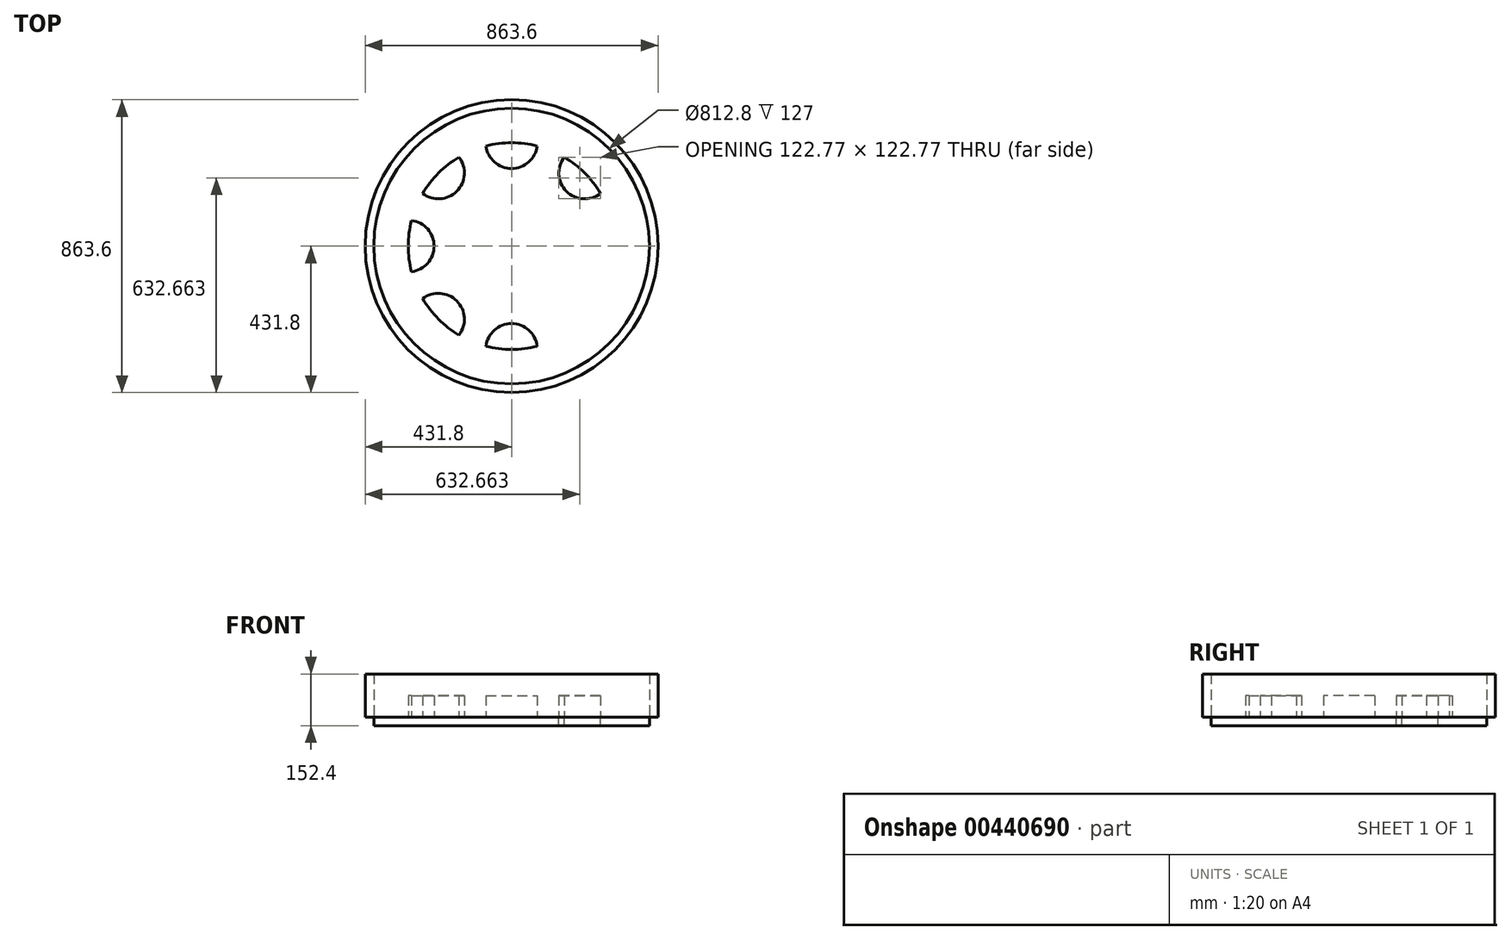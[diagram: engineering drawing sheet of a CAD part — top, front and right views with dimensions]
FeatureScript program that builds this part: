
annotation { "Feature Type Name" : "Feature", "Feature Type Description" : "" }
export const myFeature = defineFeature(function(context is Context, id is Id, definition is map)
    precondition{}
    {
        {
            var Q0;
            Q0=qCreatedBy(makeId("Top.planeOp"),FACE);
            var sketch = newSketch(context, id + "F0", { "sketchPlane" : qUnion([Q0])});
            skCircle(sketch, "E0", {"center": v(0, 0) * mm, "radius": 304.8 * mm});
            skSolve(sketch);
        }
        {
            var Q0;
            Q0=makeQuery(id+"F0.imprint","IMPRINT",FACE,{"disambiguationData":[TD([[makeQuery(id+"F0.imprint","IMPRINT",EDGE,{"derivedFrom":sQuery(id+"F0.wireOp",EDGE,"E0")}),1.0]])]});
            extrude(context, id + "F1", {"entities" : qUnion([Q0]), "depth" : 63.5 * mm});
        }
        {
            var Q0;
            Q0=makeQuery(id+"F1.opExtrude","CAP_FACE",FACE,{"disambiguationData":[OSD([sQuery(id+"F0.wireOp",EDGE,"E0")])],"isStart":true});
            var sketch = newSketch(context, id + "F2", { "sketchPlane" : qUnion([Q0])});
            skCircle(sketch, "E1", {"center": v(0, 304.8) * mm, "radius": 76.2 * mm});
            skCircle(sketch, "E2.1.0", {"center": v(215.53, 215.53) * mm, "radius": 76.2 * mm});
            skCircle(sketch, "E2.2.0", {"center": v(304.8, 0) * mm, "radius": 76.2 * mm});
            skPoint(sketch, "E2.center", {"position": v(0, 0) * mm});
            skLineSegment(sketch, "E2.anchor1", {"start": v(0, 0) * mm, "end": v(0, 304.8) * mm, "construction": true});
            skLineSegment(sketch, "E2.anchor2", {"start": v(0, 0) * mm, "end": v(304.8, 0) * mm, "construction": true});
            skCircle(sketch, "E3.1.0", {"center": v(215.53, -215.53) * mm, "radius": 76.2 * mm});
            skCircle(sketch, "E3.2.0", {"center": v(0, -304.8) * mm, "radius": 76.2 * mm});
            skLineSegment(sketch, "E3.anchor2", {"start": v(0, 0) * mm, "end": v(0, -304.8) * mm, "construction": true});
            skCircle(sketch, "E4.MirrorC", {"center": v(-215.53, 215.53) * mm, "radius": 76.2 * mm});
            skCircle(sketch, "E5.MirrorC", {"center": v(-304.8, 0) * mm, "radius": 76.2 * mm});
            skCircle(sketch, "E6.MirrorC", {"center": v(-215.53, -215.53) * mm, "radius": 76.2 * mm});
            skSolve(sketch);
        }
        {
            var Q0;
            {var subQ0=sQuery(id+"F2.wireOp",EDGE,"E1");var subQ1=makeQuery(id+"F1.opExtrude","CAP_EDGE",EDGE,{"disambiguationData":[OSD([sQuery(id+"F0.wireOp",EDGE,"E0")])],"isStart":true});var subQ2=makeQuery(id+"F2.imprint","INTERSECT",VERTEX,{"disambiguationData":[OD(0.0)],"derivedFrom":[subQ1,subQ0]});Q0=makeQuery(id+"F2.imprint","IMPRINT",FACE,{"disambiguationData":[TD([[makeQuery(id+"F2.imprint","IMPRINT",EDGE,{"disambiguationData":[TD([[subQ2,-1.0]])],"derivedFrom":subQ0}),-1.0]])]});}
            var Q1;
            {var subQ0=sQuery(id+"F2.wireOp",EDGE,"E4.MirrorC");var subQ1=makeQuery(id+"F1.opExtrude","CAP_EDGE",EDGE,{"disambiguationData":[OSD([sQuery(id+"F0.wireOp",EDGE,"E0")])],"isStart":true});var subQ2=makeQuery(id+"F2.imprint","INTERSECT",VERTEX,{"disambiguationData":[OD(0.0)],"derivedFrom":[subQ1,subQ0]});Q1=makeQuery(id+"F2.imprint","IMPRINT",FACE,{"disambiguationData":[TD([[makeQuery(id+"F2.imprint","IMPRINT",EDGE,{"disambiguationData":[TD([[subQ2,-1.0]])],"derivedFrom":subQ0}),-1.0]])]});}
            var Q2;
            {var subQ0=sQuery(id+"F2.wireOp",EDGE,"E5.MirrorC");var subQ1=makeQuery(id+"F1.opExtrude","CAP_EDGE",EDGE,{"disambiguationData":[OSD([sQuery(id+"F0.wireOp",EDGE,"E0")])],"isStart":true});var subQ2=makeQuery(id+"F2.imprint","INTERSECT",VERTEX,{"disambiguationData":[OD(0.0)],"derivedFrom":[subQ1,subQ0]});Q2=makeQuery(id+"F2.imprint","IMPRINT",FACE,{"disambiguationData":[TD([[makeQuery(id+"F2.imprint","IMPRINT",EDGE,{"disambiguationData":[TD([[subQ2,-1.0]])],"derivedFrom":subQ0}),-1.0]])]});}
            var Q3;
            {var subQ0=sQuery(id+"F2.wireOp",EDGE,"E6.MirrorC");var subQ1=makeQuery(id+"F1.opExtrude","CAP_EDGE",EDGE,{"disambiguationData":[OSD([sQuery(id+"F0.wireOp",EDGE,"E0")])],"isStart":true});var subQ2=makeQuery(id+"F2.imprint","INTERSECT",VERTEX,{"disambiguationData":[OD(0.0)],"derivedFrom":[subQ1,subQ0]});Q3=makeQuery(id+"F2.imprint","IMPRINT",FACE,{"disambiguationData":[TD([[makeQuery(id+"F2.imprint","IMPRINT",EDGE,{"disambiguationData":[TD([[subQ2,-1.0]])],"derivedFrom":subQ0}),-1.0]])]});}
            var Q4;
            {var subQ0=sQuery(id+"F2.wireOp",EDGE,"E3.2.0");var subQ1=makeQuery(id+"F1.opExtrude","CAP_EDGE",EDGE,{"disambiguationData":[OSD([sQuery(id+"F0.wireOp",EDGE,"E0")])],"isStart":true});var subQ2=makeQuery(id+"F2.imprint","INTERSECT",VERTEX,{"disambiguationData":[OD(0.0)],"derivedFrom":[subQ1,subQ0]});Q4=makeQuery(id+"F2.imprint","IMPRINT",FACE,{"disambiguationData":[TD([[makeQuery(id+"F2.imprint","IMPRINT",EDGE,{"disambiguationData":[TD([[subQ2,-1.0]])],"derivedFrom":subQ0}),1.0]])]});}
            var Q5;
            {var subQ0=sQuery(id+"F2.wireOp",EDGE,"E3.1.0");var subQ1=makeQuery(id+"F1.opExtrude","CAP_EDGE",EDGE,{"disambiguationData":[OSD([sQuery(id+"F0.wireOp",EDGE,"E0")])],"isStart":true});var subQ2=makeQuery(id+"F2.imprint","INTERSECT",VERTEX,{"disambiguationData":[OD(0.0)],"derivedFrom":[subQ1,subQ0]});Q5=makeQuery(id+"F2.imprint","IMPRINT",FACE,{"disambiguationData":[TD([[makeQuery(id+"F2.imprint","IMPRINT",EDGE,{"disambiguationData":[TD([[subQ2,-1.0]])],"derivedFrom":subQ0}),1.0]])]});}
            var Q6;
            {var subQ0=sQuery(id+"F2.wireOp",EDGE,"E2.2.0");var subQ1=makeQuery(id+"F1.opExtrude","CAP_EDGE",EDGE,{"disambiguationData":[OSD([sQuery(id+"F0.wireOp",EDGE,"E0")])],"isStart":true});var subQ2=makeQuery(id+"F2.imprint","INTERSECT",VERTEX,{"disambiguationData":[OD(0.0)],"derivedFrom":[subQ1,subQ0]});Q6=makeQuery(id+"F2.imprint","IMPRINT",FACE,{"disambiguationData":[TD([[makeQuery(id+"F2.imprint","IMPRINT",EDGE,{"disambiguationData":[TD([[subQ2,-1.0]])],"derivedFrom":subQ0}),1.0]])]});}
            var Q7;
            {var subQ0=sQuery(id+"F2.wireOp",EDGE,"E2.1.0");var subQ1=makeQuery(id+"F1.opExtrude","CAP_EDGE",EDGE,{"disambiguationData":[OSD([sQuery(id+"F0.wireOp",EDGE,"E0")])],"isStart":true});var subQ2=makeQuery(id+"F2.imprint","INTERSECT",VERTEX,{"disambiguationData":[OD(0.0)],"derivedFrom":[subQ1,subQ0]});Q7=makeQuery(id+"F2.imprint","IMPRINT",FACE,{"disambiguationData":[TD([[makeQuery(id+"F2.imprint","IMPRINT",EDGE,{"disambiguationData":[TD([[subQ2,-1.0]])],"derivedFrom":subQ0}),1.0]])]});}
            extrude(context, id + "F3", {"entities" : qUnion([Q0, Q1, Q2, Q3, Q4, Q5, Q6, Q7]), "operationType" : NewBodyOperationType.REMOVE, "oppositeDirection" : true, "depth" : 480.06 * mm});
        }
        {
            var Q0;
            Q0=makeQuery(id+"F1.opExtrude","CAP_FACE",FACE,{"disambiguationData":[OSD([sQuery(id+"F0.wireOp",EDGE,"E0")])],"isStart":true});
            var sketch = newSketch(context, id + "F4", { "sketchPlane" : qUnion([Q0])});
            skCircle(sketch, "E7", {"center": v(0, 0) * mm, "radius": 406.4 * mm});
            skSolve(sketch);
        }
        {
            var Q0;
            Q0=makeQuery(id+"F4.imprint","IMPRINT",FACE,{"disambiguationData":[TD([[makeQuery(id+"F4.imprint","IMPRINT",EDGE,{"derivedFrom":sQuery(id+"F4.wireOp",EDGE,"E7")}),1.0]])]});
            var sketch = newSketch(context, id + "F5", { "sketchPlane" : qUnion([Q0])});
            skCircle(sketch, "E8", {"center": v(0, 0) * mm, "radius": 431.8 * mm});
            skSolve(sketch);
        }
        {
            var Q0;
            {var subQ8=sQuery(id+"F2.wireOp",EDGE,"E2.1.0");Q0=makeQuery(id+"F5.imprint","IMPRINT",FACE,{"disambiguationData":[TD([[makeQuery(id+"F5.imprint","IMPRINT",EDGE,{"derivedFrom":makeQuery(id+"F4.imprint","IMPRINT",EDGE,{"derivedFrom":makeQuery(id+"F3.boolean.opBoolean","COPY",EDGE,{"derivedFrom":makeQuery(id+"F3.opExtrude","CAP_EDGE",EDGE,{"disambiguationData":[OSD([subQ8])],"isStart":true})})})}),-1.0]])]});}
            var Q1;
            Q1=makeQuery(id+"F5.imprint","IMPRINT",FACE,{"disambiguationData":[TD([[makeQuery(id+"F5.imprint","IMPRINT",EDGE,{"derivedFrom":makeQuery(id+"F4.imprint","IMPRINT",EDGE,{"derivedFrom":sQuery(id+"F4.wireOp",EDGE,"E7")})}),1.0]])]});
            extrude(context, id + "F6", {"entities" : qUnion([Q0, Q1]), "operationType" : NewBodyOperationType.ADD, "depth" : 25.4 * mm});
        }
        {
            var Q0;
            Q0=makeQuery(id+"F5.imprint","IMPRINT",FACE,{"disambiguationData":[TD([[makeQuery(id+"F5.imprint","IMPRINT",EDGE,{"derivedFrom":sQuery(id+"F5.wireOp",EDGE,"E8")}),1.0]])]});
            extrude(context, id + "F7", {"entities" : qUnion([Q0]), "oppositeDirection" : true, "depth" : 127 * mm});
        }
    });
